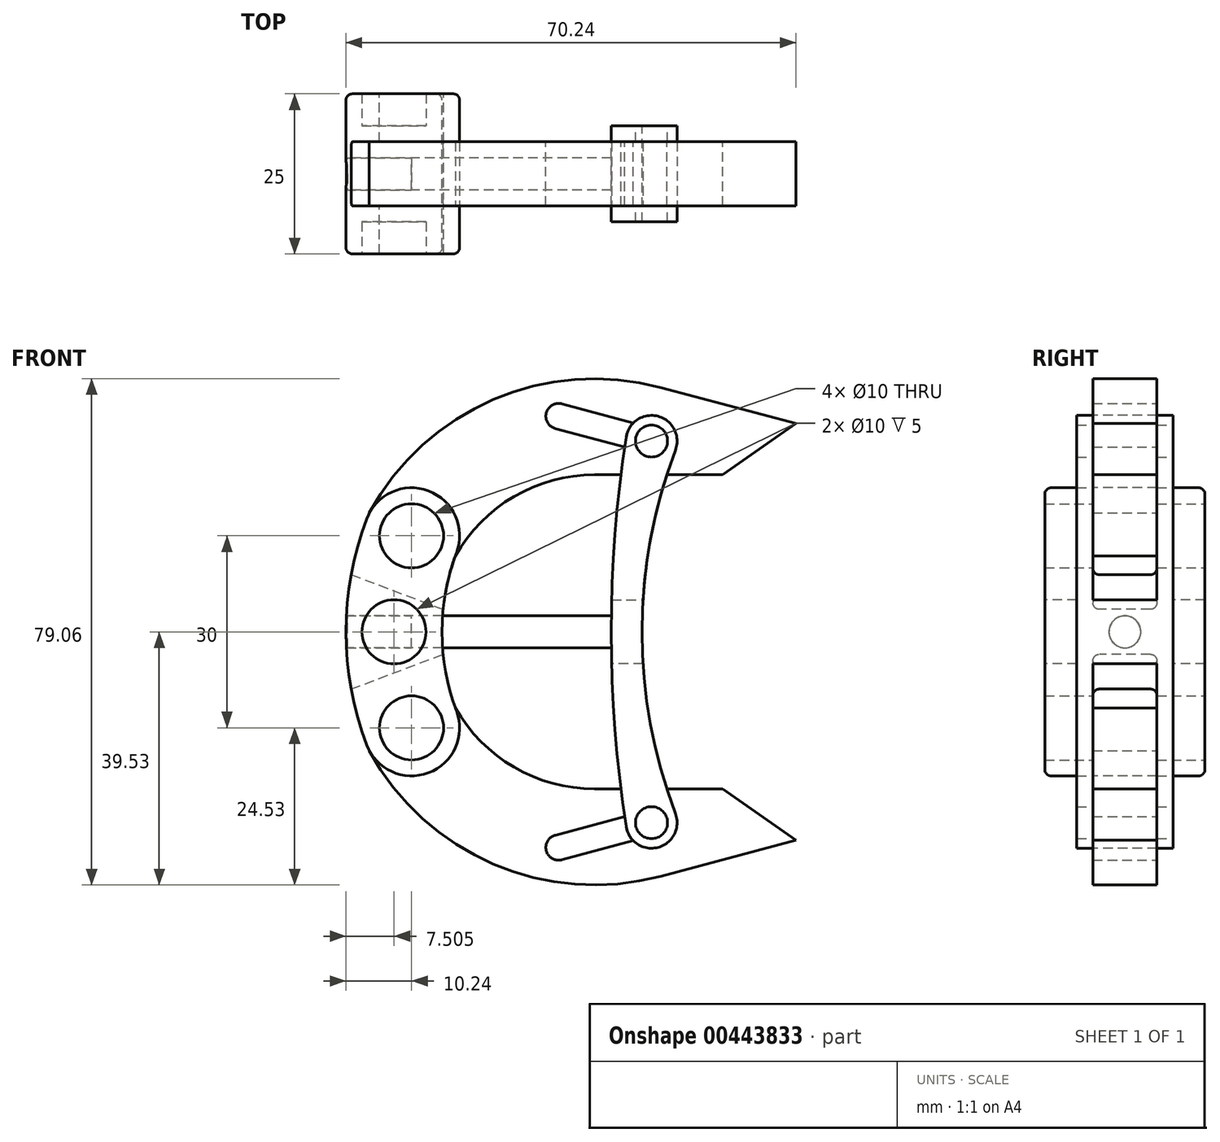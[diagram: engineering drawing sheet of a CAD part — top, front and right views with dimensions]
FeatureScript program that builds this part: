
annotation { "Feature Type Name" : "Feature", "Feature Type Description" : "" }
export const myFeature = defineFeature(function(context is Context, id is Id, definition is map)
    precondition{}
    {
        {
            var Q0;
            Q0=qCreatedBy(makeId("Front.planeOp"),FACE);
            var sketch = newSketch(context, id + "F0", { "sketchPlane" : qUnion([Q0])});
            skLineSegment(sketch, "E0", {"start": v(0, 15) * mm, "end": v(0, -15) * mm, "construction": true});
            skLineSegment(sketch, "E1", {"start": v(0, 0) * mm, "end": v(80, 0) * mm, "construction": true});
            skCircle(sketch, "E2", {"center": v(0, 15) * mm, "radius": 5 * mm});
            skCircle(sketch, "E3", {"center": v(0, -15) * mm, "radius": 5 * mm});
            skArc(sketch, "E4.0", {"start": v(7.02, 12.35) * mm, "mid": v(2.65, 22.02) * mm, "end": v(-7.02, 17.65) * mm});
            skArc(sketch, "E5.0", {"start": v(-7.02, -17.65) * mm, "mid": v(2.65, -22.02) * mm, "end": v(7.02, -12.35) * mm});
            skArc(sketch, "E6", {"start": v(-7.02, 17.65) * mm, "mid": v(-10.24, 0) * mm, "end": v(-7.02, -17.65) * mm});
            skArc(sketch, "E7", {"start": v(7.02, 12.35) * mm, "mid": v(4.76, 0) * mm, "end": v(7.02, -12.35) * mm});
            skSolve(sketch);
        }
        {
            var Q0;
            Q0=qCreatedBy(makeId("Front.planeOp"),FACE);
            var sketch = newSketch(context, id + "F1", { "sketchPlane" : qUnion([Q0])});
            skCircle(sketch, "E8.0.0", {"center": v(0, 15) * mm, "radius": 5 * mm});
            skArc(sketch, "E9", {"start": v(-6.6, 18.57) * mm, "mid": v(-3.57, 8.4) * mm, "end": v(6.6, 11.43) * mm});
            skArc(sketch, "E10", {"start": v(38.92, 38.17) * mm, "mid": v(12.76, 36.27) * mm, "end": v(-6.6, 18.57) * mm});
            skArc(sketch, "E11", {"start": v(28.58, 24.53) * mm, "mid": v(15.79, 21) * mm, "end": v(6.6, 11.43) * mm});
            skLineSegment(sketch, "E12", {"start": v(28.58, 24.53) * mm, "end": v(48.58, 24.53) * mm});
            skArc(sketch, "E13", {"start": v(23.48, 35.6) * mm, "mid": v(21.03, 34.2) * mm, "end": v(22.44, 31.75) * mm});
            skArc(sketch, "E14", {"start": v(36.93, 27.87) * mm, "mid": v(39.38, 29.28) * mm, "end": v(37.97, 31.73) * mm});
            skLineSegment(sketch, "E15", {"start": v(22.96, 33.68) * mm, "end": v(37.45, 29.8) * mm, "construction": true});
            skLineSegment(sketch, "E16", {"start": v(23.48, 35.6) * mm, "end": v(37.97, 31.73) * mm});
            skLineSegment(sketch, "E17", {"start": v(22.44, 31.75) * mm, "end": v(36.93, 27.87) * mm});
            skLineSegment(sketch, "E18", {"start": v(38.92, 38.17) * mm, "end": v(37.45, 29.8) * mm, "construction": true});
            skLineSegment(sketch, "E19", {"start": v(38.92, 38.17) * mm, "end": v(60, 32.53) * mm});
            skLineSegment(sketch, "E20", {"start": v(48.58, 24.53) * mm, "end": v(60, 32.53) * mm});
            skArc(sketch, "E21.MirrorCS", {"start": v(36.93, -27.87) * mm, "mid": v(39.38, -29.28) * mm, "end": v(37.97, -31.73) * mm});
            skLineSegment(sketch, "E22.MirrorCS", {"start": v(22.44, -31.75) * mm, "end": v(36.93, -27.87) * mm});
            skArc(sketch, "E23.MirrorCS", {"start": v(23.48, -35.6) * mm, "mid": v(21.03, -34.2) * mm, "end": v(22.44, -31.75) * mm});
            skLineSegment(sketch, "E24.MirrorCS", {"start": v(23.48, -35.6) * mm, "end": v(37.97, -31.73) * mm});
            skCircle(sketch, "E25.MirrorC", {"center": v(0, -15) * mm, "radius": 5 * mm});
            skLineSegment(sketch, "E26.MirrorCS", {"start": v(28.58, -24.53) * mm, "end": v(48.58, -24.53) * mm});
            skArc(sketch, "E27.MirrorCS", {"start": v(28.58, -24.53) * mm, "mid": v(15.79, -21) * mm, "end": v(6.6, -11.43) * mm});
            skArc(sketch, "E28.MirrorCS", {"start": v(-6.6, -18.57) * mm, "mid": v(-3.57, -8.4) * mm, "end": v(6.6, -11.43) * mm});
            skArc(sketch, "E29.MirrorCS", {"start": v(38.92, -38.17) * mm, "mid": v(12.76, -36.27) * mm, "end": v(-6.6, -18.57) * mm});
            skLineSegment(sketch, "E30.MirrorCS", {"start": v(48.58, -24.53) * mm, "end": v(60, -32.53) * mm});
            skLineSegment(sketch, "E31.MirrorCS", {"start": v(38.92, -38.17) * mm, "end": v(60, -32.53) * mm});
            skSolve(sketch);
        }
        {
            var Q0;
            Q0 = qSketchRegion(id + "F1", true);
            extrude(context, id + "F2", {"entities" : qUnion([Q0]), "endBound" : BoundingType.SYMMETRIC, "depth" : 10 * mm});
        }
        {
            var Q0;
            Q0=makeQuery(id+"F0.imprint","IMPRINT",FACE,{"disambiguationData":[TD([[makeQuery(id+"F0.imprint","IMPRINT",EDGE,{"derivedFrom":sQuery(id+"F0.wireOp",EDGE,"E2")}),-1.0]])]});
            extrude(context, id + "F3", {"entities" : qUnion([Q0]), "endBound" : BoundingType.SYMMETRIC, "depth" : 25 * mm});
        }
        {
            var Q0;
            Q0=makeQuery(id+"F3.opExtrude","CAP_FACE",FACE,{"disambiguationData":[OSD([sQuery(id+"F0.wireOp",EDGE,"E2"),sQuery(id+"F0.wireOp",EDGE,"E3"),sQuery(id+"F0.wireOp",EDGE,"E4.0"),sQuery(id+"F0.wireOp",EDGE,"E5.0"),sQuery(id+"F0.wireOp",EDGE,"E6"),sQuery(id+"F0.wireOp",EDGE,"E7")])],"isStart":false});
            var sketch = newSketch(context, id + "F4", { "sketchPlane" : qUnion([Q0])});
            skArc(sketch, "E32", {"start": v(0, 15) * mm, "mid": v(-2.74, 0) * mm, "end": v(0, -15) * mm, "construction": true});
            skCircle(sketch, "E33", {"center": v(-2.74, 0) * mm, "radius": 5 * mm});
            skSolve(sketch);
        }
        {
            var Q0;
            Q0 = qSketchRegion(id + "F4", true);
            extrude(context, id + "F5", {"entities" : qUnion([Q0]), "operationType" : NewBodyOperationType.REMOVE, "endBound" : BoundingType.THROUGH_ALL, "oppositeDirection" : true, "depth" : 25 * mm});
        }
        {
            var Q0;
            Q0=qCreatedBy(makeId("Front.planeOp"),FACE);
            var sketch = newSketch(context, id + "F6", { "sketchPlane" : qUnion([Q0])});
            skCircle(sketch, "E34", {"center": v(0, -15) * mm, "radius": 9 * mm, "construction": true});
            skLineSegment(sketch, "E35", {"start": v(-9.43, 8.94) * mm, "end": v(4.94, 3.52) * mm});
            skCircle(sketch, "E36.0", {"center": v(-2.74, 0) * mm, "radius": 6 * mm, "construction": true});
            skArc(sketch, "E37.0", {"start": v(7.02, 12.35) * mm, "mid": v(5.7, 8) * mm, "end": v(4.94, 3.52) * mm});
            skArc(sketch, "E37.1", {"start": v(7.02, 12.35) * mm, "mid": v(2.65, 22.02) * mm, "end": v(-7.02, 17.65) * mm});
            skArc(sketch, "E38.trimOffspring", {"start": v(4.94, -3.52) * mm, "mid": v(5.7, -8) * mm, "end": v(7.02, -12.35) * mm});
            skArc(sketch, "E39.0", {"start": v(-7.02, 17.65) * mm, "mid": v(-8.42, 13.35) * mm, "end": v(-9.43, 8.94) * mm});
            skArc(sketch, "E40.trimOffspring", {"start": v(-9.43, -8.94) * mm, "mid": v(-8.42, -13.35) * mm, "end": v(-7.02, -17.65) * mm});
            skCircle(sketch, "E41.0", {"center": v(-2.74, 0) * mm, "radius": 5 * mm});
            skLineSegment(sketch, "E42", {"start": v(-9.43, -8.94) * mm, "end": v(4.94, -3.52) * mm});
            skArc(sketch, "E43", {"start": v(-9.43, 8.94) * mm, "mid": v(-10.24, 0) * mm, "end": v(-9.43, -8.94) * mm, "construction": true});
            skArc(sketch, "E44", {"start": v(4.97, -3.82) * mm, "mid": v(5.73, -8.15) * mm, "end": v(7.02, -12.35) * mm});
            skArc(sketch, "E45", {"start": v(4.94, 3.52) * mm, "mid": v(4.77, -0.15) * mm, "end": v(4.97, -3.82) * mm, "construction": true});
            skArc(sketch, "E46.0", {"start": v(-7.02, -17.65) * mm, "mid": v(2.65, -22.02) * mm, "end": v(7.02, -12.35) * mm});
            skSolve(sketch);
        }
        {
            var Q0;
            Q0=makeQuery(id+"F6.imprint","IMPRINT",FACE,{"disambiguationData":[TD([[makeQuery(id+"F6.imprint","IMPRINT",EDGE,{"derivedFrom":sQuery(id+"F6.wireOp",EDGE,"E38.trimOffspring")}),-1.0]])]});
            var Q1;
            Q1=makeQuery(id+"F6.imprint","IMPRINT",FACE,{"disambiguationData":[TD([[makeQuery(id+"F6.imprint","IMPRINT",EDGE,{"derivedFrom":sQuery(id+"F6.wireOp",EDGE,"E35")}),1.0]])]});
            extrude(context, id + "F7", {"entities" : qUnion([Q0, Q1]), "operationType" : NewBodyOperationType.REMOVE, "endBound" : BoundingType.SYMMETRIC, "oppositeDirection" : true, "depth" : 10 * mm});
        }
        {
            var Q0;
            Q0=qCreatedBy(makeId("Front.planeOp"),FACE);
            var sketch = newSketch(context, id + "F8", { "sketchPlane" : qUnion([Q0])});
            skCircle(sketch, "E47.0", {"center": v(-2.74, 0) * mm, "radius": 5 * mm});
            skSolve(sketch);
        }
        {
            var Q0;
            Q0 = qSketchRegion(id + "F8", true);
            var Q1;
            Q1=sQuery(id+"F8.wireOp",EDGE,"E47.0");
            extrude(context, id + "F9", {"entities" : qUnion([Q0]), "operationType" : NewBodyOperationType.ADD, "surfaceEntities" : qUnion([Q1]), "endBound" : BoundingType.SYMMETRIC, "depth" : 15 * mm});
        }
        {
            var Q0;
            Q0=qCreatedBy(makeId("Right.planeOp"),FACE);
            var sketch = newSketch(context, id + "F10", { "sketchPlane" : qUnion([Q0])});
            skCircle(sketch, "E48", {"center": v(0, 0) * mm, "radius": 2.5 * mm});
            skSolve(sketch);
        }
        {
            var Q0;
            Q0 = qSketchRegion(id + "F10", true);
            extrude(context, id + "F11", {"entities" : qUnion([Q0]), "operationType" : NewBodyOperationType.REMOVE, "endBound" : BoundingType.THROUGH_ALL, "oppositeDirection" : true, "depth" : 25 * mm});
        }
        {
            var Q0;
            Q0=qCreatedBy(makeId("Right.planeOp"),FACE);
            var sketch = newSketch(context, id + "F12", { "sketchPlane" : qUnion([Q0])});
            skCircle(sketch, "E49.0", {"center": v(0, 0) * mm, "radius": 2.5 * mm});
            skSolve(sketch);
        }
        {
            var Q0;
            Q0 = qSketchRegion(id + "F12", true);
            var Q1;
            Q1 = qSketchRegion(id + "F14", true);
            extrude(context, id + "F13", {"entities" : qUnion([Q0, Q1]), "depth" : 33.3 * mm, "hasSecondDirection" : true, "secondDirectionOppositeDirection" : true, "secondDirectionDepth" : 10 * mm});
        }
        {
            var Q0;
            Q0=qCreatedBy(makeId("Front.planeOp"),FACE);
            var sketch = newSketch(context, id + "F14", { "sketchPlane" : qUnion([Q0])});
            skArc(sketch, "E50.0", {"start": v(36.93, -27.87) * mm, "mid": v(39.38, -29.28) * mm, "end": v(37.97, -31.73) * mm});
            skArc(sketch, "E50.1", {"start": v(23.48, -35.6) * mm, "mid": v(21.03, -34.2) * mm, "end": v(22.44, -31.75) * mm});
            skArc(sketch, "E50.2", {"start": v(36.93, 27.87) * mm, "mid": v(39.38, 29.28) * mm, "end": v(37.97, 31.73) * mm});
            skArc(sketch, "E50.3", {"start": v(23.48, 35.6) * mm, "mid": v(21.03, 34.2) * mm, "end": v(22.44, 31.75) * mm});
            skArc(sketch, "E51", {"start": v(41.19, 28.38) * mm, "mid": v(38.47, 33.67) * mm, "end": v(33.5, 30.4) * mm});
            skArc(sketch, "E52", {"start": v(33.5, -30.4) * mm, "mid": v(38.47, -33.67) * mm, "end": v(41.19, -28.38) * mm});
            skArc(sketch, "E53", {"start": v(33.5, 30.4) * mm, "mid": v(31.17, 0) * mm, "end": v(33.5, -30.4) * mm});
            skArc(sketch, "E54", {"start": v(41.19, 28.38) * mm, "mid": v(35.99, 0) * mm, "end": v(41.19, -28.38) * mm});
            skCircle(sketch, "E55", {"center": v(37.45, 29.8) * mm, "radius": 2.5 * mm});
            skCircle(sketch, "E56", {"center": v(37.45, -29.8) * mm, "radius": 2.5 * mm});
            skSolve(sketch);
        }
        {
            var Q0;
            Q0 = qSketchRegion(id + "F14", true);
            extrude(context, id + "F15", {"entities" : qUnion([Q0]), "operationType" : NewBodyOperationType.ADD, "endBound" : BoundingType.SYMMETRIC, "depth" : 15 * mm});
        }
        {
            var Q0;
            Q0=qCreatedBy(makeId("Front.planeOp"),FACE);
            var sketch = newSketch(context, id + "F16", { "sketchPlane" : qUnion([Q0])});
            skLineSegment(sketch, "E57", {"start": v(24.12, 0) * mm, "end": v(49.26, 0) * mm, "construction": true});
            skArc(sketch, "E58.0.0", {"start": v(33.5, 30.4) * mm, "mid": v(31.96, 17.74) * mm, "end": v(31.23, 5) * mm});
            skArc(sketch, "E58.0.1", {"start": v(33.5, -30.4) * mm, "mid": v(38.47, -33.67) * mm, "end": v(41.19, -28.38) * mm});
            skArc(sketch, "E58.0.2", {"start": v(41.19, -28.38) * mm, "mid": v(37.79, -16.88) * mm, "end": v(36.14, -5) * mm});
            skArc(sketch, "E58.0.3", {"start": v(41.19, 28.38) * mm, "mid": v(38.47, 33.67) * mm, "end": v(33.5, 30.4) * mm});
            skLineSegment(sketch, "E59", {"start": v(31.23, 5) * mm, "end": v(36.14, 5) * mm});
            skLineSegment(sketch, "E60", {"start": v(36.14, -5) * mm, "end": v(31.23, -5) * mm});
            skArc(sketch, "E61.trimOffspring", {"start": v(36.14, 5) * mm, "mid": v(37.79, 16.88) * mm, "end": v(41.19, 28.38) * mm});
            skArc(sketch, "E62.trimOffspring", {"start": v(31.23, -5) * mm, "mid": v(31.96, -17.74) * mm, "end": v(33.5, -30.4) * mm});
            skSolve(sketch);
        }
        {
            var Q0;
            Q0 = qSketchRegion(id + "F16", true);
            extrude(context, id + "F17", {"entities" : qUnion([Q0]), "operationType" : NewBodyOperationType.REMOVE, "endBound" : BoundingType.SYMMETRIC, "oppositeDirection" : true, "depth" : 10 * mm});
        }
        {
            var Q0;
            Q0=makeQuery(id+"F3.opExtrude","CAP_EDGE",EDGE,{"disambiguationData":[OSD([sQuery(id+"F0.wireOp",EDGE,"E5.0")])],"isStart":false});
            var Q1;
            Q1=makeQuery(id+"F3.opExtrude","CAP_EDGE",EDGE,{"disambiguationData":[OSD([sQuery(id+"F0.wireOp",EDGE,"E4.0")])],"isStart":false});
            var Q2;
            Q2=makeQuery(id+"F3.opExtrude","CAP_EDGE",EDGE,{"disambiguationData":[OSD([sQuery(id+"F0.wireOp",EDGE,"E5.0")])],"isStart":true});
            var Q3;
            Q3=makeQuery(id+"F7.boolean.opBoolean","COPY",EDGE,{"derivedFrom":makeQuery(id+"F7.opExtrude","SWEPT_EDGE",EDGE,{"disambiguationData":[OSD([sQuery(id+"F6.wireOp",EDGE,"E35"),sQuery(id+"F6.wireOp",EDGE,"E37.0")])]})});
            var Q4;
            Q4=makeQuery(id+"F7.boolean.opBoolean","COPY",EDGE,{"derivedFrom":makeQuery(id+"F7.opExtrude","SWEPT_EDGE",EDGE,{"disambiguationData":[OSD([sQuery(id+"F6.wireOp",EDGE,"E38.trimOffspring"),sQuery(id+"F6.wireOp",EDGE,"E42")])]})});
            var Q5;
            Q5=makeQuery(id+"F7.boolean.opBoolean","COPY",EDGE,{"derivedFrom":makeQuery(id+"F7.opExtrude","CAP_EDGE",EDGE,{"disambiguationData":[OSD([sQuery(id+"F6.wireOp",EDGE,"E35")])],"isStart":false})});
            var Q6;
            Q6=makeQuery(id+"F7.boolean.opBoolean","COPY",EDGE,{"derivedFrom":makeQuery(id+"F7.opExtrude","CAP_EDGE",EDGE,{"disambiguationData":[OSD([sQuery(id+"F6.wireOp",EDGE,"E35")])],"isStart":true})});
            var Q7;
            Q7=makeQuery(id+"F7.boolean.opBoolean","COPY",EDGE,{"derivedFrom":makeQuery(id+"F7.opExtrude","CAP_EDGE",EDGE,{"disambiguationData":[OSD([sQuery(id+"F6.wireOp",EDGE,"E42")])],"isStart":true})});
            var Q8;
            Q8=makeQuery(id+"F7.boolean.opBoolean","COPY",EDGE,{"derivedFrom":makeQuery(id+"F7.opExtrude","CAP_EDGE",EDGE,{"disambiguationData":[OSD([sQuery(id+"F6.wireOp",EDGE,"E42")])],"isStart":false})});
            fillet(context, id + "F18", {"entities" : qUnion([Q0, Q1, Q2, Q3, Q4, Q5, Q6, Q7, Q8]), "radius" : 1 * mm, "tangentPropagation" : true, "allowEdgeOverflow" : false});
        }
    });
